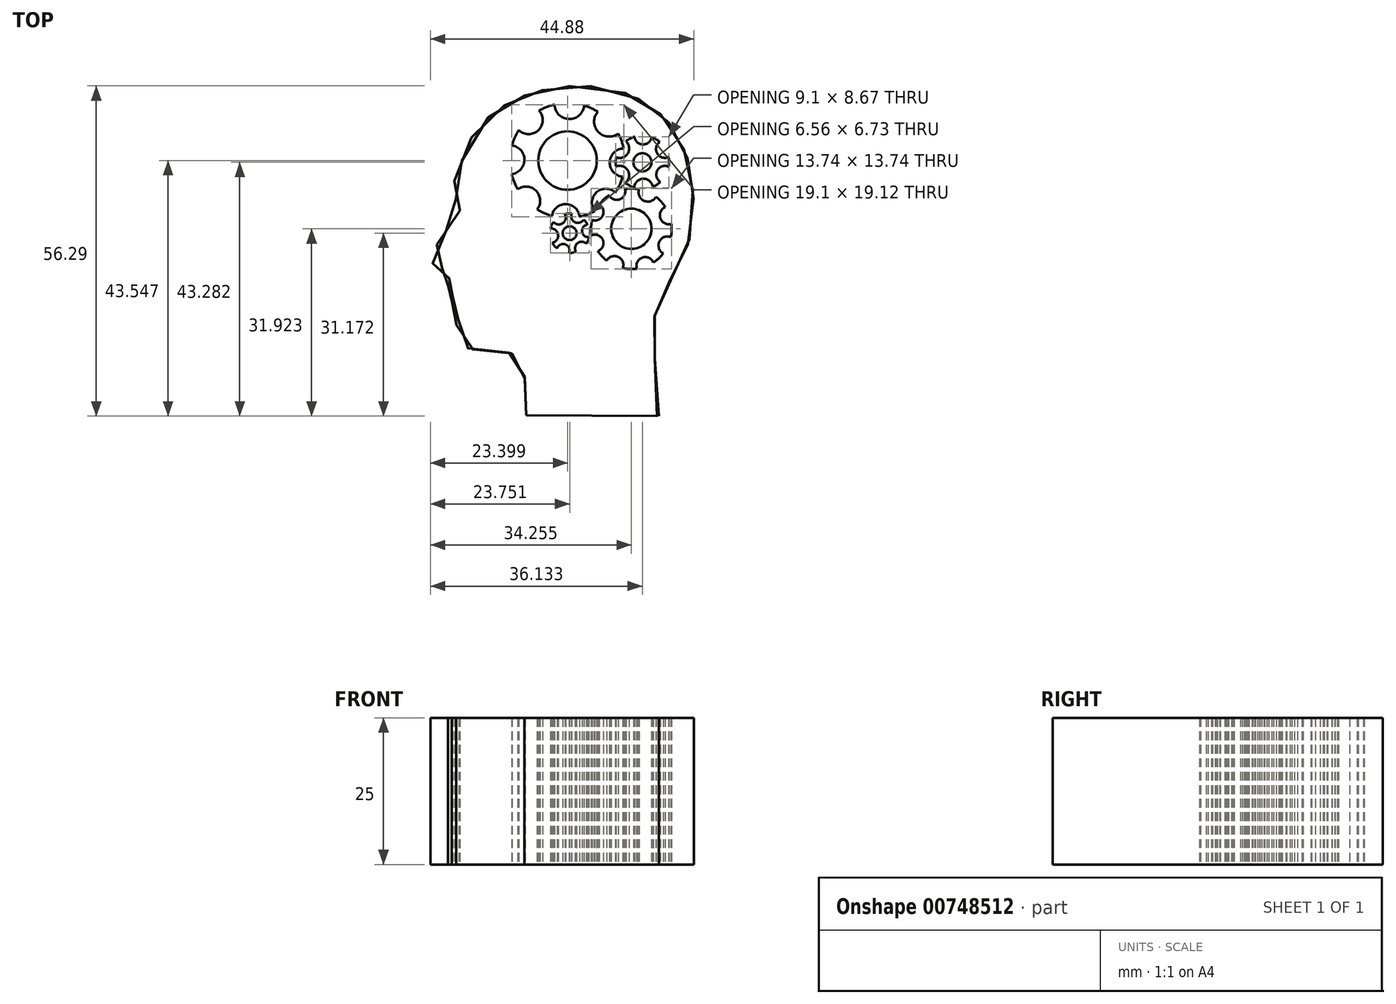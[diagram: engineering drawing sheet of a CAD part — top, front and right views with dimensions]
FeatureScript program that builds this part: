
annotation { "Feature Type Name" : "Feature", "Feature Type Description" : "" }
export const myFeature = defineFeature(function(context is Context, id is Id, definition is map)
    precondition{}
    {
        {
            var Q0;
            Q0=qCreatedBy(makeId("Top.planeOp"),FACE);
            var sketch = newSketch(context, id + "F0", { "sketchPlane" : qUnion([Q0])});
            skFitSpline(sketch, "E0", {"points": [v(-58.45, -34.79) * mm, v(-58.47, -34.78) * mm, v(-58.71, -32.78) * mm, v(-58.78, -30.5) * mm, v(-58.73, -28.04) * mm, v(-58.75, -26.48) * mm, v(-59.35, -25.42) * mm, v(-60.48, -24.5) * mm, v(-62.15, -23.93) * mm, v(-65.13, -23.77) * mm, v(-67.45, -23.61) * mm, v(-69.1, -23.01) * mm, v(-70.1, -21.68) * mm, v(-70.4, -20.1) * mm, v(-70.06, -18.27) * mm, v(-70.09, -16.91) * mm, v(-70.53, -16.56) * mm, v(-71, -15.91) * mm, v(-71.14, -15.4) * mm, v(-71, -14.73) * mm, v(-70.72, -14.55) * mm, v(-70.68, -14.05) * mm, v(-71.07, -13.8) * mm, v(-71.58, -13.17) * mm, v(-71.79, -12.5) * mm, v(-71.46, -10.97) * mm, v(-71.33, -10.25) * mm, v(-71.44, -9.98) * mm, v(-72.61, -9.74) * mm, v(-74.1, -9.17) * mm, v(-74.76, -8.27) * mm, v(-74.65, -7.37) * mm, v(-73.24, -4.98) * mm, v(-71.51, -2.5) * mm, v(-69.9, -0.23) * mm, v(-69.8, 0.47) * mm, v(-70.34, 1.75) * mm, v(-70.94, 3.08) * mm, v(-70.78, 4.97) * mm, v(-69.77, 7.76) * mm, v(-68.37, 11.34) * mm, v(-66.44, 14.5) * mm, v(-63.62, 17.07) * mm, v(-61.76, 18.3) * mm, v(-59.43, 19.45) * mm, v(-56.73, 20.37) * mm, v(-53.77, 21.01) * mm, v(-50.52, 21.33) * mm, v(-45.58, 21.18) * mm, v(-41.77, 20.2) * mm, v(-38.83, 18.88) * mm, v(-37.16, 17.86) * mm, v(-35.28, 16.24) * mm, v(-33.6, 14.35) * mm, v(-32.42, 12.33) * mm, v(-31.2, 9.69) * mm, v(-30.47, 6.82) * mm, v(-30.2, 4.58) * mm, v(-29.92, 1.8) * mm, v(-30.16, -1.8) * mm, v(-30.75, -5.06) * mm, v(-31.63, -7.35) * mm, v(-33.06, -10.35) * mm, v(-34.42, -12.71) * mm, v(-35.34, -14.28) * mm, v(-36.28, -16.66) * mm, v(-36.72, -18.63) * mm, v(-36.79, -20.9) * mm, v(-36.6, -24.12) * mm, v(-36.33, -29.19) * mm, v(-35.83, -34.91) * mm, v(-35.86, -34.93) * mm, v(-58.45, -34.79) * mm]});
            skCircle(sketch, "E1", {"center": v(-51.43, 8.63) * mm, "radius": 4.98 * mm});
            skCircle(sketch, "E2", {"center": v(-38.67, 8.34) * mm, "radius": 1.54 * mm});
            skCircle(sketch, "E3", {"center": v(-40.55, -3) * mm, "radius": 3.43 * mm});
            skCircle(sketch, "E4", {"center": v(-51.07, -3.76) * mm, "radius": 1.18 * mm});
            skArc(sketch, "E5", {"start": v(-56.6, 0.3) * mm, "mid": v(-55.39, -0.33) * mm, "end": v(-54.1, -0.8) * mm});
            skArc(sketch, "E6", {"start": v(-60.95, 6.31) * mm, "mid": v(-60.52, 4.98) * mm, "end": v(-59.91, 3.73) * mm});
            skArc(sketch, "E7", {"start": v(-59.74, 13.82) * mm, "mid": v(-60.4, 12.56) * mm, "end": v(-60.88, 11.21) * mm});
            skArc(sketch, "E8", {"start": v(-53.65, 18.18) * mm, "mid": v(-55, 17.76) * mm, "end": v(-56.28, 17.15) * mm});
            skArc(sketch, "E9", {"start": v(-46.28, 16.97) * mm, "mid": v(-47.4, 17.57) * mm, "end": v(-48.6, 18.01) * mm});
            skArc(sketch, "E10", {"start": v(-41.85, 10.7) * mm, "mid": v(-42.23, 12) * mm, "end": v(-42.78, 13.23) * mm});
            skArc(sketch, "E11", {"start": v(-43.28, 3.19) * mm, "mid": v(-42.56, 4.48) * mm, "end": v(-42.03, 5.87) * mm});
            skArc(sketch, "E12", {"start": v(-49.37, -0.94) * mm, "mid": v(-48.04, -0.56) * mm, "end": v(-46.78, 0) * mm});
            skArc(sketch, "E13", {"start": v(-59.74, 13.82) * mm, "mid": v(-56.4, 13.8) * mm, "end": v(-56.28, 17.15) * mm});
            skArc(sketch, "E14", {"start": v(-53.65, 18.18) * mm, "mid": v(-51.2, 15.7) * mm, "end": v(-48.6, 18.01) * mm});
            skArc(sketch, "E15", {"start": v(-46.28, 16.97) * mm, "mid": v(-46.2, 13.53) * mm, "end": v(-42.78, 13.23) * mm});
            skArc(sketch, "E16", {"start": v(-41.85, 10.7) * mm, "mid": v(-44.23, 8.37) * mm, "end": v(-42.03, 5.87) * mm});
            skArc(sketch, "E17", {"start": v(-43.28, 3.19) * mm, "mid": v(-46.5, 3.21) * mm, "end": v(-46.78, 0) * mm});
            skArc(sketch, "E18", {"start": v(-49.37, -0.94) * mm, "mid": v(-51.67, 1.2) * mm, "end": v(-54.1, -0.8) * mm});
            skArc(sketch, "E19", {"start": v(-56.6, 0.3) * mm, "mid": v(-56.77, 3.46) * mm, "end": v(-59.91, 3.73) * mm});
            skArc(sketch, "E20", {"start": v(-60.95, 6.31) * mm, "mid": v(-58.78, 8.73) * mm, "end": v(-60.88, 11.21) * mm});
            skArc(sketch, "E21", {"start": v(-40.01, 12.69) * mm, "mid": v(-40.78, 12.37) * mm, "end": v(-41.48, 11.92) * mm});
            skArc(sketch, "E22", {"start": v(-35.71, 11.8) * mm, "mid": v(-36.37, 12.27) * mm, "end": v(-37.1, 12.62) * mm});
            skArc(sketch, "E23", {"start": v(-34.18, 7.58) * mm, "mid": v(-34.12, 8.41) * mm, "end": v(-34.2, 9.24) * mm});
            skArc(sketch, "E24", {"start": v(-36.9, 4.15) * mm, "mid": v(-36.21, 4.51) * mm, "end": v(-35.6, 4.98) * mm});
            skArc(sketch, "E25", {"start": v(-41.57, 4.84) * mm, "mid": v(-40.86, 4.36) * mm, "end": v(-40.07, 4.01) * mm});
            skArc(sketch, "E26", {"start": v(-43.14, 9.19) * mm, "mid": v(-43.22, 8.4) * mm, "end": v(-43.16, 7.63) * mm});
            skArc(sketch, "E27", {"start": v(-40.01, 12.69) * mm, "mid": v(-38.6, 11.38) * mm, "end": v(-37.1, 12.62) * mm});
            skArc(sketch, "E28", {"start": v(-35.71, 11.8) * mm, "mid": v(-36.14, 9.83) * mm, "end": v(-34.2, 9.24) * mm});
            skArc(sketch, "E29", {"start": v(-34.18, 7.58) * mm, "mid": v(-36.12, 6.95) * mm, "end": v(-35.6, 4.98) * mm});
            skArc(sketch, "E30", {"start": v(-36.9, 4.15) * mm, "mid": v(-38.55, 5.53) * mm, "end": v(-40.07, 4.01) * mm});
            skArc(sketch, "E31", {"start": v(-41.57, 4.84) * mm, "mid": v(-41.14, 6.93) * mm, "end": v(-43.16, 7.63) * mm});
            skArc(sketch, "E32", {"start": v(-43.14, 9.19) * mm, "mid": v(-41.16, 9.86) * mm, "end": v(-41.48, 11.92) * mm});
            skArc(sketch, "E33", {"start": v(-44.34, 2.72) * mm, "mid": v(-45.25, 2) * mm, "end": v(-46.04, 1.12) * mm});
            skArc(sketch, "E34", {"start": v(-47.25, -1.5) * mm, "mid": v(-47.41, -2.8) * mm, "end": v(-47.32, -4.12) * mm});
            skArc(sketch, "E35", {"start": v(-46.26, -6.82) * mm, "mid": v(-45.57, -7.69) * mm, "end": v(-44.76, -8.43) * mm});
            skArc(sketch, "E36", {"start": v(-42, -9.72) * mm, "mid": v(-40.82, -9.87) * mm, "end": v(-39.63, -9.81) * mm});
            skArc(sketch, "E37", {"start": v(-36.8, -8.76) * mm, "mid": v(-35.89, -8.05) * mm, "end": v(-35.11, -7.2) * mm});
            skArc(sketch, "E38", {"start": v(-33.82, -4.41) * mm, "mid": v(-33.68, -3.3) * mm, "end": v(-33.73, -2.18) * mm});
            skArc(sketch, "E39", {"start": v(-34.77, 0.72) * mm, "mid": v(-35.49, 1.64) * mm, "end": v(-36.35, 2.43) * mm});
            skArc(sketch, "E40", {"start": v(-39.24, 3.74) * mm, "mid": v(-40.44, 3.86) * mm, "end": v(-41.65, 3.77) * mm});
            skArc(sketch, "E41", {"start": v(-44.34, 2.72) * mm, "mid": v(-42.51, 2.02) * mm, "end": v(-41.65, 3.77) * mm});
            skArc(sketch, "E42", {"start": v(-39.24, 3.74) * mm, "mid": v(-38.39, 1.77) * mm, "end": v(-36.35, 2.43) * mm});
            skArc(sketch, "E43", {"start": v(-34.77, 0.72) * mm, "mid": v(-35.6, -1.22) * mm, "end": v(-33.73, -2.18) * mm});
            skArc(sketch, "E44", {"start": v(-33.82, -4.41) * mm, "mid": v(-35.79, -5.2) * mm, "end": v(-35.11, -7.2) * mm});
            skArc(sketch, "E45", {"start": v(-36.8, -8.76) * mm, "mid": v(-38.71, -7.93) * mm, "end": v(-39.63, -9.81) * mm});
            skArc(sketch, "E46", {"start": v(-42, -9.72) * mm, "mid": v(-42.8, -7.8) * mm, "end": v(-44.76, -8.43) * mm});
            skArc(sketch, "E47", {"start": v(-46.26, -6.82) * mm, "mid": v(-45.4, -4.92) * mm, "end": v(-47.32, -4.12) * mm});
            skArc(sketch, "E48", {"start": v(-47.25, -1.5) * mm, "mid": v(-45.43, -0.75) * mm, "end": v(-46.04, 1.12) * mm});
            skArc(sketch, "E49", {"start": v(-50.73, -0.4) * mm, "mid": v(-51.31, -0.4) * mm, "end": v(-51.9, -0.5) * mm});
            skArc(sketch, "E50", {"start": v(-48.04, -2.3) * mm, "mid": v(-48.3, -1.83) * mm, "end": v(-48.65, -1.42) * mm});
            skArc(sketch, "E51", {"start": v(-48.22, -5.55) * mm, "mid": v(-47.94, -5) * mm, "end": v(-47.77, -4.42) * mm});
            skArc(sketch, "E52", {"start": v(-51.18, -7.12) * mm, "mid": v(-50.58, -7.09) * mm, "end": v(-49.98, -6.94) * mm});
            skArc(sketch, "E53", {"start": v(-54.01, -5.39) * mm, "mid": v(-53.66, -5.9) * mm, "end": v(-53.22, -6.35) * mm});
            skArc(sketch, "E54", {"start": v(-53.84, -1.85) * mm, "mid": v(-54.13, -2.36) * mm, "end": v(-54.33, -2.92) * mm});
            skArc(sketch, "E55", {"start": v(-53.84, -1.85) * mm, "mid": v(-52.25, -2.06) * mm, "end": v(-51.9, -0.5) * mm});
            skArc(sketch, "E56", {"start": v(-50.73, -0.4) * mm, "mid": v(-50.16, -1.88) * mm, "end": v(-48.65, -1.42) * mm});
            skArc(sketch, "E57", {"start": v(-48.04, -2.3) * mm, "mid": v(-48.95, -3.5) * mm, "end": v(-47.77, -4.42) * mm});
            skArc(sketch, "E58", {"start": v(-48.22, -5.55) * mm, "mid": v(-49.72, -5.46) * mm, "end": v(-49.98, -6.94) * mm});
            skArc(sketch, "E59", {"start": v(-51.18, -7.12) * mm, "mid": v(-51.8, -5.66) * mm, "end": v(-53.22, -6.35) * mm});
            skArc(sketch, "E60", {"start": v(-54.01, -5.39) * mm, "mid": v(-53.04, -4.01) * mm, "end": v(-54.33, -2.92) * mm});
            skSolve(sketch);
        }
        {
            var Q0;
            Q0=makeQuery(id+"F0.imprint","IMPRINT",FACE,{"disambiguationData":[TD([[makeQuery(id+"F0.imprint","IMPRINT",EDGE,{"derivedFrom":sQuery(id+"F0.wireOp",EDGE,"E0")}),-1.0]])]});
            var Q1;
            Q1=makeQuery(id+"F0.imprint","IMPRINT",FACE,{"disambiguationData":[TD([[makeQuery(id+"F0.imprint","IMPRINT",EDGE,{"derivedFrom":sQuery(id+"F0.wireOp",EDGE,"E1")}),1.0]])]});
            var Q2;
            Q2=makeQuery(id+"F0.imprint","IMPRINT",FACE,{"disambiguationData":[TD([[makeQuery(id+"F0.imprint","IMPRINT",EDGE,{"derivedFrom":sQuery(id+"F0.wireOp",EDGE,"E2")}),1.0]])]});
            var Q3;
            Q3=makeQuery(id+"F0.imprint","IMPRINT",FACE,{"disambiguationData":[TD([[makeQuery(id+"F0.imprint","IMPRINT",EDGE,{"derivedFrom":sQuery(id+"F0.wireOp",EDGE,"E3")}),1.0]])]});
            var Q4;
            Q4=makeQuery(id+"F0.imprint","IMPRINT",FACE,{"disambiguationData":[TD([[makeQuery(id+"F0.imprint","IMPRINT",EDGE,{"derivedFrom":sQuery(id+"F0.wireOp",EDGE,"E4")}),1.0]])]});
            extrude(context, id + "F1", {"entities" : qUnion([Q0, Q1, Q2, Q3, Q4]), "depth" : 25 * mm, "offsetDistance" : 25 * mm});
        }
    });
